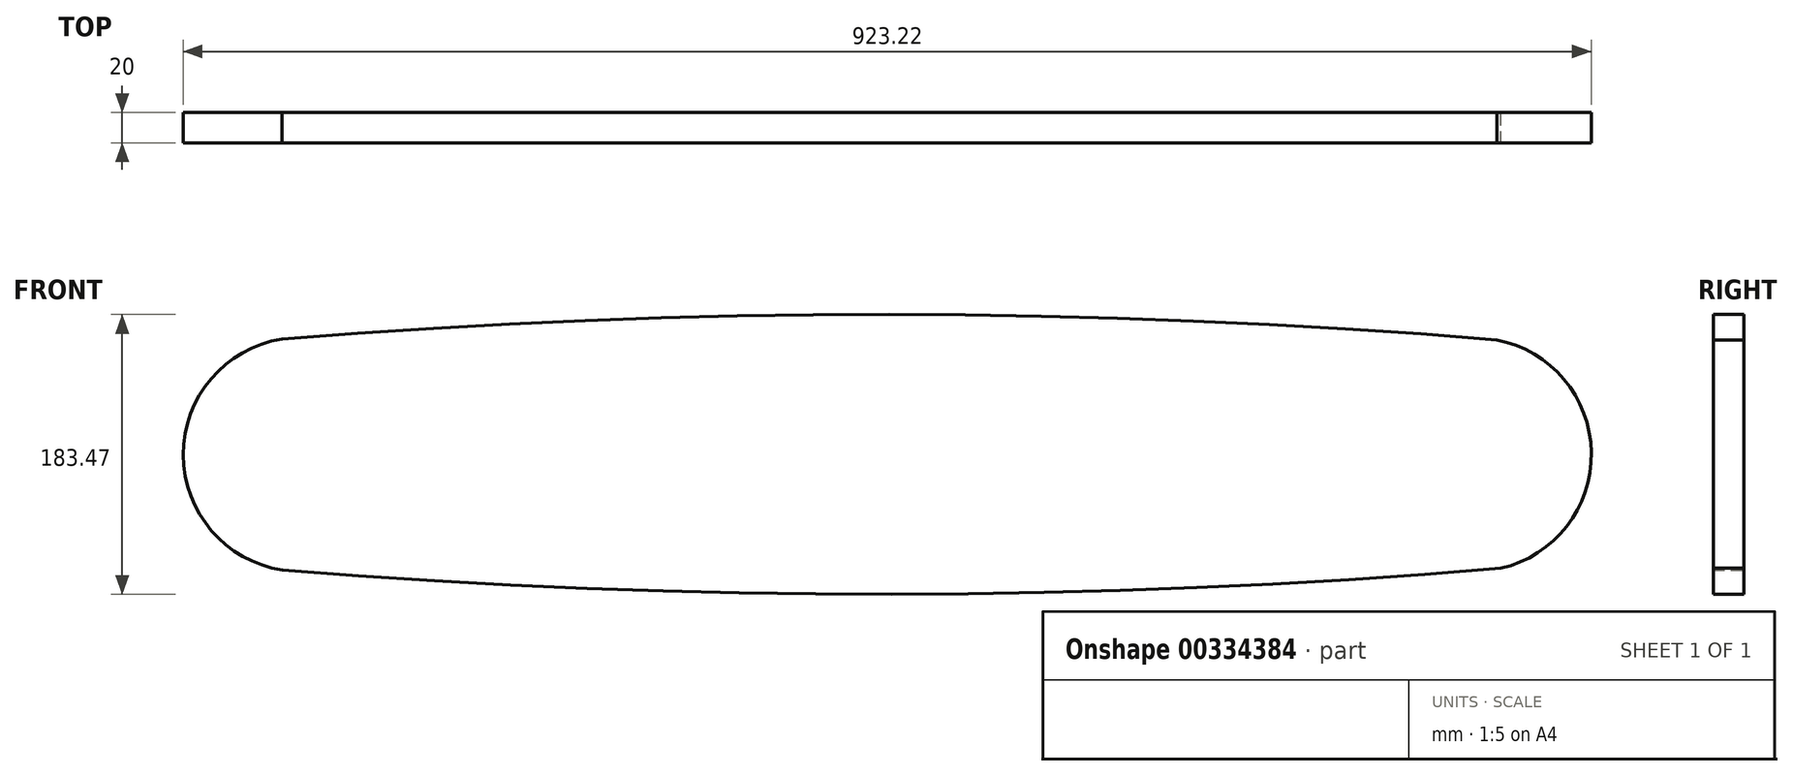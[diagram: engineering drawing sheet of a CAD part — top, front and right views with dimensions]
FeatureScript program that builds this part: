
annotation { "Feature Type Name" : "Feature", "Feature Type Description" : "" }
export const myFeature = defineFeature(function(context is Context, id is Id, definition is map)
    precondition{}
    {
        {
            var Q0;
            Q0=qCreatedBy(makeId("Front.planeOp"),FACE);
            var sketch = newSketch(context, id + "F0", { "sketchPlane" : qUnion([Q0])});
            skCircle(sketch, "E0", {"center": v(-49.12, 0) * mm, "radius": 76.61 * mm});
            skCircle(sketch, "E1", {"center": v(720.88, 0) * mm, "radius": 76.61 * mm});
            skLineSegment(sketch, "E2", {"start": v(-49.12, 0) * mm, "end": v(720.88, 0) * mm});
            skArc(sketch, "E3", {"start": v(-60.72, -75.73) * mm, "mid": v(338.78, -91.65) * mm, "end": v(738.22, -74.62) * mm});
            skArc(sketch, "E4", {"start": v(735.58, 75.19) * mm, "mid": v(337.25, 91.81) * mm, "end": v(-61.1, 75.67) * mm});
            skSolve(sketch);
        }
        {
            var Q0;
            {var subQ1=sQuery(id+"F0.wireOp",EDGE,"E0");var subQ4=sQuery(id+"F0.wireOp",EDGE,"E4");var subQ5=makeQuery(id+"F0.imprint","INTERSECT",VERTEX,{"disambiguationData":[OD(1.0)],"derivedFrom":[subQ1,subQ4]});Q0=makeQuery(id+"F0.imprint","IMPRINT",FACE,{"disambiguationData":[TD([[makeQuery(id+"F0.imprint","IMPRINT",EDGE,{"disambiguationData":[TD([[subQ5,1.0]])],"derivedFrom":subQ1}),1.0]])]});}
            var Q1;
            {var subQ0=sQuery(id+"F0.wireOp",EDGE,"E4");var subQ1=sQuery(id+"F0.wireOp",EDGE,"E0");var subQ2=makeQuery(id+"F0.imprint","INTERSECT",VERTEX,{"disambiguationData":[OD(1.0)],"derivedFrom":[subQ1,subQ0]});Q1=makeQuery(id+"F0.imprint","IMPRINT",FACE,{"disambiguationData":[TD([[makeQuery(id+"F0.imprint","IMPRINT",EDGE,{"disambiguationData":[TD([[subQ2,1.0]])],"derivedFrom":subQ1}),-1.0]])]});}
            var Q2;
            {var subQ0=sQuery(id+"F0.wireOp",EDGE,"E2");var subQ1=sQuery(id+"F0.wireOp",EDGE,"E0");var subQ2=makeQuery(id+"F0.imprint","INTERSECT",VERTEX,{"derivedFrom":[subQ1,subQ0]});Q2=makeQuery(id+"F0.imprint","IMPRINT",FACE,{"disambiguationData":[TD([[makeQuery(id+"F0.imprint","IMPRINT",EDGE,{"disambiguationData":[TD([[subQ2,1.0]])],"derivedFrom":subQ1}),-1.0]])]});}
            var Q3;
            {var subQ1=sQuery(id+"F0.wireOp",EDGE,"E1");var subQ4=sQuery(id+"F0.wireOp",EDGE,"E4");var subQ7=makeQuery(id+"F0.imprint","INTERSECT",VERTEX,{"disambiguationData":[OD(1.0)],"derivedFrom":[subQ1,subQ4]});Q3=makeQuery(id+"F0.imprint","IMPRINT",FACE,{"disambiguationData":[TD([[makeQuery(id+"F0.imprint","IMPRINT",EDGE,{"disambiguationData":[TD([[subQ7,-1.0]])],"derivedFrom":subQ1}),1.0]])]});}
            extrude(context, id + "F1", {"entities" : qUnion([Q0, Q1, Q2, Q3]), "depth" : 20 * mm});
        }
    });
